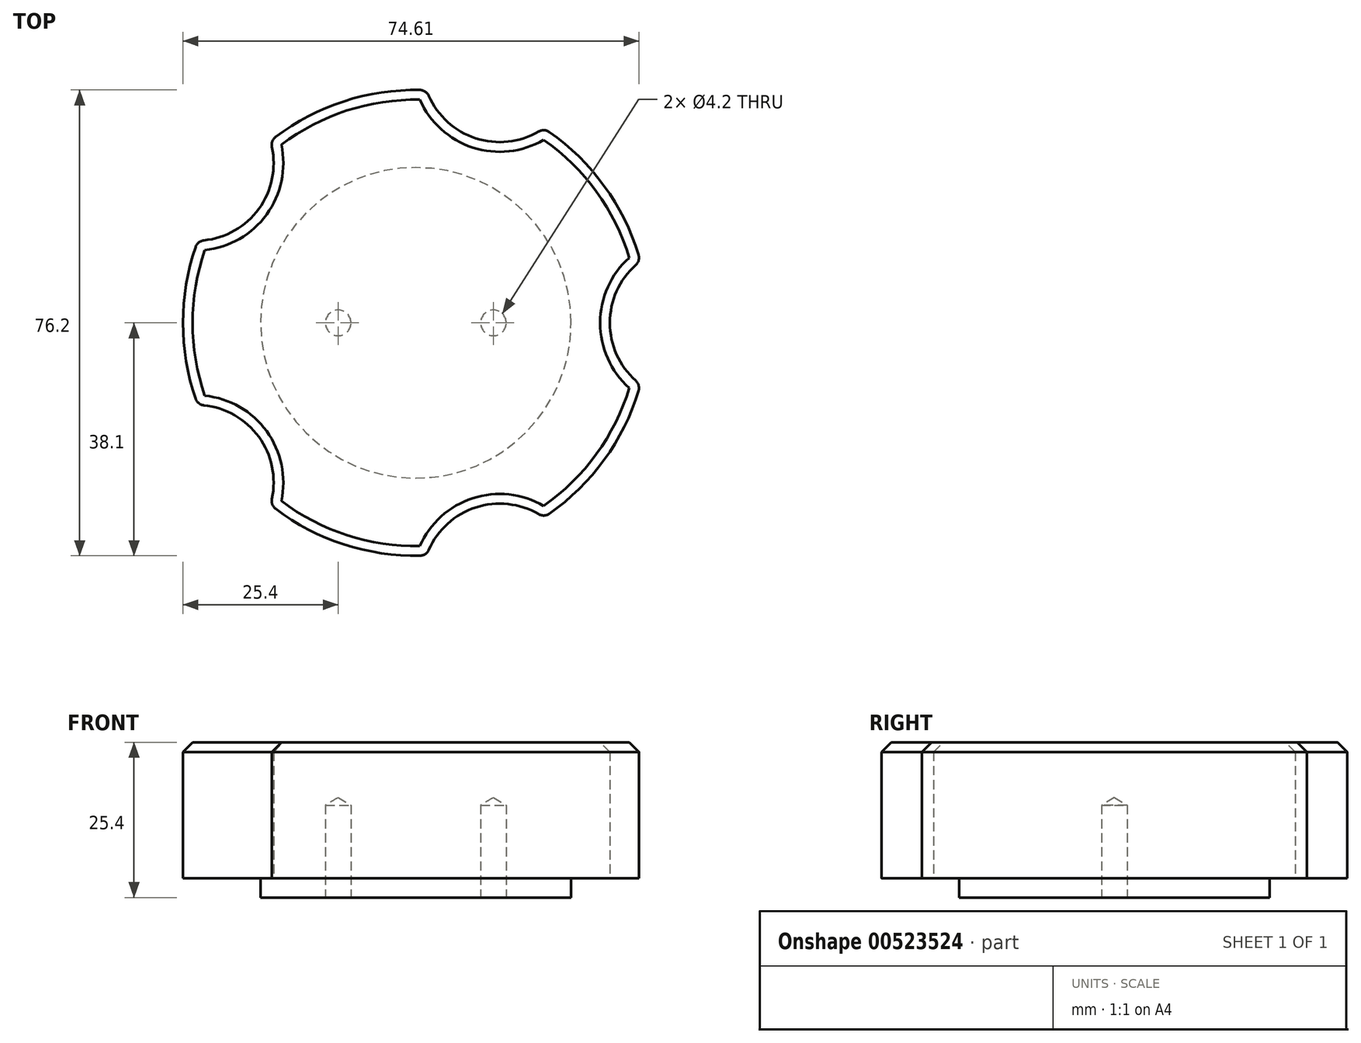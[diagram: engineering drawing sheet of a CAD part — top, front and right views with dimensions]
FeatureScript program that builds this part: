
annotation { "Feature Type Name" : "Feature", "Feature Type Description" : "" }
export const myFeature = defineFeature(function(context is Context, id is Id, definition is map)
    precondition{}
    {
        {
            var Q0;
            Q0=qCreatedBy(makeId("Front.planeOp"),FACE);
            var sketch = newSketch(context, id + "F0", { "sketchPlane" : qUnion([Q0])});
            skLineSegment(sketch, "E0.bottom", {"start": v(0, 0) * mm, "end": v(25.4, 0) * mm});
            skLineSegment(sketch, "E0.top", {"start": v(0, 25.4) * mm, "end": v(38.1, 25.4) * mm});
            skLineSegment(sketch, "E0.left", {"start": v(0, 0) * mm, "end": v(0, 25.4) * mm});
            skLineSegment(sketch, "E0.right", {"start": v(38.1, 3.18) * mm, "end": v(38.1, 25.4) * mm});
            skLineSegment(sketch, "E1.bottom", {"start": v(25.4, 3.18) * mm, "end": v(38.1, 3.18) * mm});
            skLineSegment(sketch, "E1.left", {"start": v(25.4, 3.18) * mm, "end": v(25.4, 0) * mm});
            skSolve(sketch);
        }
        {
            var Q0;
            Q0=makeQuery(id+"F0.imprint","IMPRINT",FACE,{"disambiguationData":[TD([[makeQuery(id+"F0.imprint","IMPRINT",EDGE,{"derivedFrom":sQuery(id+"F0.wireOp",EDGE,"E0.bottom")}),1.0]])]});
            var Q1;
            Q1=sQuery(id+"F0.wireOp",EDGE,"E0.left");
            revolve(context, id + "F1", {"entities" : qUnion([Q0]), "axis" : qUnion([Q1]), "revolveType" : RevolveType.FULL});
        }
        {
            var Q0;
            Q0=qCreatedBy(makeId("Top.planeOp"),FACE);
            var sketch = newSketch(context, id + "F2", { "sketchPlane" : qUnion([Q0])});
            skCircle(sketch, "E2", {"center": v(44.45, 0) * mm, "radius": 12.7 * mm});
            skSolve(sketch);
        }
        {
            var Q0;
            Q0=makeQuery(id+"F2.imprint","IMPRINT",FACE,{"disambiguationData":[TD([[makeQuery(id+"F2.imprint","IMPRINT",EDGE,{"derivedFrom":sQuery(id+"F2.wireOp",EDGE,"E2")}),1.0]])]});
            extrude(context, id + "F3", {"entities" : qUnion([Q0]), "depth" : 50.8 * mm, "offsetDistance" : 25.4 * mm});
        }
        {
            var Q0;
            Q0=makeQuery(id+"F3.opExtrude","SWEPT_BODY",BODY,{"disambiguationData":[OSD([sQuery(id+"F2.wireOp",EDGE,"E2")])]});
            var Q1;
            Q1=makeQuery(id+"F1.opRevolve","SWEPT_FACE",FACE,{"disambiguationData":[OSD([sQuery(id+"F0.wireOp",EDGE,"E0.right")])]});
            circularPattern(context, id + "F4", {"entities" : qUnion([Q0]), "axis" : qUnion([Q1]), "angle" : 360 * degree, "instanceCount" : 5, "equalSpace" : true});
        }
        {
            var Q0;
            Q0=makeQuery(id+"F4.opPattern","COPY",BODY,{"derivedFrom":makeQuery(id+"F3.opExtrude","SWEPT_BODY",BODY,{"disambiguationData":[OSD([sQuery(id+"F2.wireOp",EDGE,"E2")])]}),"instanceName":"2"});
            var Q1;
            Q1=makeQuery(id+"F4.opPattern","COPY",BODY,{"derivedFrom":makeQuery(id+"F3.opExtrude","SWEPT_BODY",BODY,{"disambiguationData":[OSD([sQuery(id+"F2.wireOp",EDGE,"E2")])]}),"instanceName":"1"});
            var Q2;
            Q2=makeQuery(id+"F3.opExtrude","SWEPT_BODY",BODY,{"disambiguationData":[OSD([sQuery(id+"F2.wireOp",EDGE,"E2")])]});
            var Q3;
            Q3=makeQuery(id+"F4.opPattern","COPY",BODY,{"derivedFrom":makeQuery(id+"F3.opExtrude","SWEPT_BODY",BODY,{"disambiguationData":[OSD([sQuery(id+"F2.wireOp",EDGE,"E2")])]}),"instanceName":"4"});
            var Q4;
            Q4=makeQuery(id+"F4.opPattern","COPY",BODY,{"derivedFrom":makeQuery(id+"F3.opExtrude","SWEPT_BODY",BODY,{"disambiguationData":[OSD([sQuery(id+"F2.wireOp",EDGE,"E2")])]}),"instanceName":"3"});
            var Q5;
            Q5=makeQuery(id+"F1.opRevolve","SWEPT_BODY",BODY,{"disambiguationData":[OSD([sQuery(id+"F0.wireOp",EDGE,"E0.bottom"),sQuery(id+"F0.wireOp",EDGE,"E0.top"),sQuery(id+"F0.wireOp",EDGE,"E0.left"),sQuery(id+"F0.wireOp",EDGE,"E0.right"),sQuery(id+"F0.wireOp",EDGE,"E1.bottom"),sQuery(id+"F0.wireOp",EDGE,"E1.left")])]});
            booleanBodies(context, id + "F5", {"operationType" : BooleanOperationType.SUBTRACTION, "tools" : qUnion([Q0, Q1, Q2, Q3, Q4]), "targets" : qUnion([Q5])});
        }
        {
            var Q0;
            Q0=makeQuery(id+"F5.opBoolean","INTERSECT",EDGE,{"disambiguationData":[OD(1.0)],"derivedFrom":[makeQuery(id+"F1.opRevolve","SWEPT_FACE",FACE,{"disambiguationData":[OSD([sQuery(id+"F0.wireOp",EDGE,"E0.right")])]}),makeQuery(id+"F4.opPattern","COPY",FACE,{"derivedFrom":makeQuery(id+"F3.opExtrude","SWEPT_FACE",FACE,{"disambiguationData":[OSD([sQuery(id+"F2.wireOp",EDGE,"E2")])]}),"instanceName":"1"})]});
            var Q1;
            Q1=makeQuery(id+"F5.opBoolean","INTERSECT",EDGE,{"disambiguationData":[OD(0.0)],"derivedFrom":[makeQuery(id+"F1.opRevolve","SWEPT_FACE",FACE,{"disambiguationData":[OSD([sQuery(id+"F0.wireOp",EDGE,"E0.right")])]}),makeQuery(id+"F4.opPattern","COPY",FACE,{"derivedFrom":makeQuery(id+"F3.opExtrude","SWEPT_FACE",FACE,{"disambiguationData":[OSD([sQuery(id+"F2.wireOp",EDGE,"E2")])]}),"instanceName":"1"})]});
            var Q2;
            Q2=makeQuery(id+"F5.opBoolean","INTERSECT",EDGE,{"disambiguationData":[OD(0.0)],"derivedFrom":[makeQuery(id+"F1.opRevolve","SWEPT_FACE",FACE,{"disambiguationData":[OSD([sQuery(id+"F0.wireOp",EDGE,"E0.right")])]}),makeQuery(id+"F3.opExtrude","SWEPT_FACE",FACE,{"disambiguationData":[OSD([sQuery(id+"F2.wireOp",EDGE,"E2")])]})]});
            var Q3;
            Q3=makeQuery(id+"F5.opBoolean","INTERSECT",EDGE,{"disambiguationData":[OD(1.0)],"derivedFrom":[makeQuery(id+"F1.opRevolve","SWEPT_FACE",FACE,{"disambiguationData":[OSD([sQuery(id+"F0.wireOp",EDGE,"E0.right")])]}),makeQuery(id+"F3.opExtrude","SWEPT_FACE",FACE,{"disambiguationData":[OSD([sQuery(id+"F2.wireOp",EDGE,"E2")])]})]});
            var Q4;
            Q4=makeQuery(id+"F5.opBoolean","INTERSECT",EDGE,{"disambiguationData":[OD(0.0)],"derivedFrom":[makeQuery(id+"F1.opRevolve","SWEPT_FACE",FACE,{"disambiguationData":[OSD([sQuery(id+"F0.wireOp",EDGE,"E0.right")])]}),makeQuery(id+"F4.opPattern","COPY",FACE,{"derivedFrom":makeQuery(id+"F3.opExtrude","SWEPT_FACE",FACE,{"disambiguationData":[OSD([sQuery(id+"F2.wireOp",EDGE,"E2")])]}),"instanceName":"4"})]});
            var Q5;
            Q5=makeQuery(id+"F5.opBoolean","INTERSECT",EDGE,{"disambiguationData":[OD(1.0)],"derivedFrom":[makeQuery(id+"F1.opRevolve","SWEPT_FACE",FACE,{"disambiguationData":[OSD([sQuery(id+"F0.wireOp",EDGE,"E0.right")])]}),makeQuery(id+"F4.opPattern","COPY",FACE,{"derivedFrom":makeQuery(id+"F3.opExtrude","SWEPT_FACE",FACE,{"disambiguationData":[OSD([sQuery(id+"F2.wireOp",EDGE,"E2")])]}),"instanceName":"4"})]});
            var Q6;
            Q6=makeQuery(id+"F5.opBoolean","INTERSECT",EDGE,{"disambiguationData":[OD(1.0)],"derivedFrom":[makeQuery(id+"F1.opRevolve","SWEPT_FACE",FACE,{"disambiguationData":[OSD([sQuery(id+"F0.wireOp",EDGE,"E0.right")])]}),makeQuery(id+"F4.opPattern","COPY",FACE,{"derivedFrom":makeQuery(id+"F3.opExtrude","SWEPT_FACE",FACE,{"disambiguationData":[OSD([sQuery(id+"F2.wireOp",EDGE,"E2")])]}),"instanceName":"3"})]});
            var Q7;
            Q7=makeQuery(id+"F5.opBoolean","INTERSECT",EDGE,{"disambiguationData":[OD(0.0)],"derivedFrom":[makeQuery(id+"F1.opRevolve","SWEPT_FACE",FACE,{"disambiguationData":[OSD([sQuery(id+"F0.wireOp",EDGE,"E0.right")])]}),makeQuery(id+"F4.opPattern","COPY",FACE,{"derivedFrom":makeQuery(id+"F3.opExtrude","SWEPT_FACE",FACE,{"disambiguationData":[OSD([sQuery(id+"F2.wireOp",EDGE,"E2")])]}),"instanceName":"3"})]});
            var Q8;
            Q8=makeQuery(id+"F5.opBoolean","INTERSECT",EDGE,{"disambiguationData":[OD(1.0)],"derivedFrom":[makeQuery(id+"F1.opRevolve","SWEPT_FACE",FACE,{"disambiguationData":[OSD([sQuery(id+"F0.wireOp",EDGE,"E0.right")])]}),makeQuery(id+"F4.opPattern","COPY",FACE,{"derivedFrom":makeQuery(id+"F3.opExtrude","SWEPT_FACE",FACE,{"disambiguationData":[OSD([sQuery(id+"F2.wireOp",EDGE,"E2")])]}),"instanceName":"2"})]});
            var Q9;
            Q9=makeQuery(id+"F5.opBoolean","INTERSECT",EDGE,{"disambiguationData":[OD(0.0)],"derivedFrom":[makeQuery(id+"F1.opRevolve","SWEPT_FACE",FACE,{"disambiguationData":[OSD([sQuery(id+"F0.wireOp",EDGE,"E0.right")])]}),makeQuery(id+"F4.opPattern","COPY",FACE,{"derivedFrom":makeQuery(id+"F3.opExtrude","SWEPT_FACE",FACE,{"disambiguationData":[OSD([sQuery(id+"F2.wireOp",EDGE,"E2")])]}),"instanceName":"2"})]});
            fillet(context, id + "F6", {"entities" : qUnion([Q0, Q1, Q2, Q3, Q4, Q5, Q6, Q7, Q8, Q9]), "radius" : 1.59 * mm, "tangentPropagation" : true, "allowEdgeOverflow" : false});
        }
        {
            var Q0;
            Q0=makeQuery(id+"F1.opRevolve","SWEPT_FACE",FACE,{"disambiguationData":[OSD([sQuery(id+"F0.wireOp",EDGE,"E0.top")])]});
            chamfer(context, id + "F7", {"entities" : qUnion([Q0]), "width" : 1.59 * mm, "tangentPropagation" : true});
        }
        {
            var Q0;
            Q0=qCreatedBy(makeId("Top.planeOp"),FACE);
            var sketch = newSketch(context, id + "F8", { "sketchPlane" : qUnion([Q0])});
            skCircle(sketch, "E3", {"center": v(0, 0) * mm, "radius": 12.7 * mm, "construction": true});
            skPoint(sketch, "E4", {"position": v(-12.7, 0) * mm});
            skPoint(sketch, "E5", {"position": v(12.7, 0) * mm});
            skSolve(sketch);
        }
        {
            var Q0;
            Q0=sQuery(id+"F8.wireOp",VERTEX,"E4");
            var Q1;
            Q1=sQuery(id+"F8.wireOp",VERTEX,"E5");
            var Q2;
            Q2=makeQuery(id+"F1.opRevolve","SWEPT_BODY",BODY,{"disambiguationData":[OSD([sQuery(id+"F0.wireOp",EDGE,"E0.bottom"),sQuery(id+"F0.wireOp",EDGE,"E0.top"),sQuery(id+"F0.wireOp",EDGE,"E0.left"),sQuery(id+"F0.wireOp",EDGE,"E0.right"),sQuery(id+"F0.wireOp",EDGE,"E1.bottom"),sQuery(id+"F0.wireOp",EDGE,"E1.left")])]});
            hole(context, id + "F9", {"style" : HoleStyle.SIMPLE, "endStyle" : HoleEndStyle.BLIND, "oppositeDirection" : true, "standardTappedOrClearance" : lookupTablePath({ "standard" : "ISO", "engagement" : "75%", "pitch" : "0.8 mm", "size" : "M5", "type" : "Tapped" }), "standardBlindInLast" : lookupTablePath({ "standard" : "ISO", "engagement" : "75%", "pitch" : "0.8 mm", "size" : "M5", "type" : "Tapped" }), "holeDiameter" : 4.2 * mm, "showTappedDepth" : true, "holeDepth" : 15.1 * mm, "isTappedThrough" : true, "tappedDepth" : 12.7 * mm, "tapClearance" : 3, "locations" : qUnion([Q0, Q1]), "scope" : qUnion([Q2]), "majorDiameter" : 5 * mm});
        }
    });
